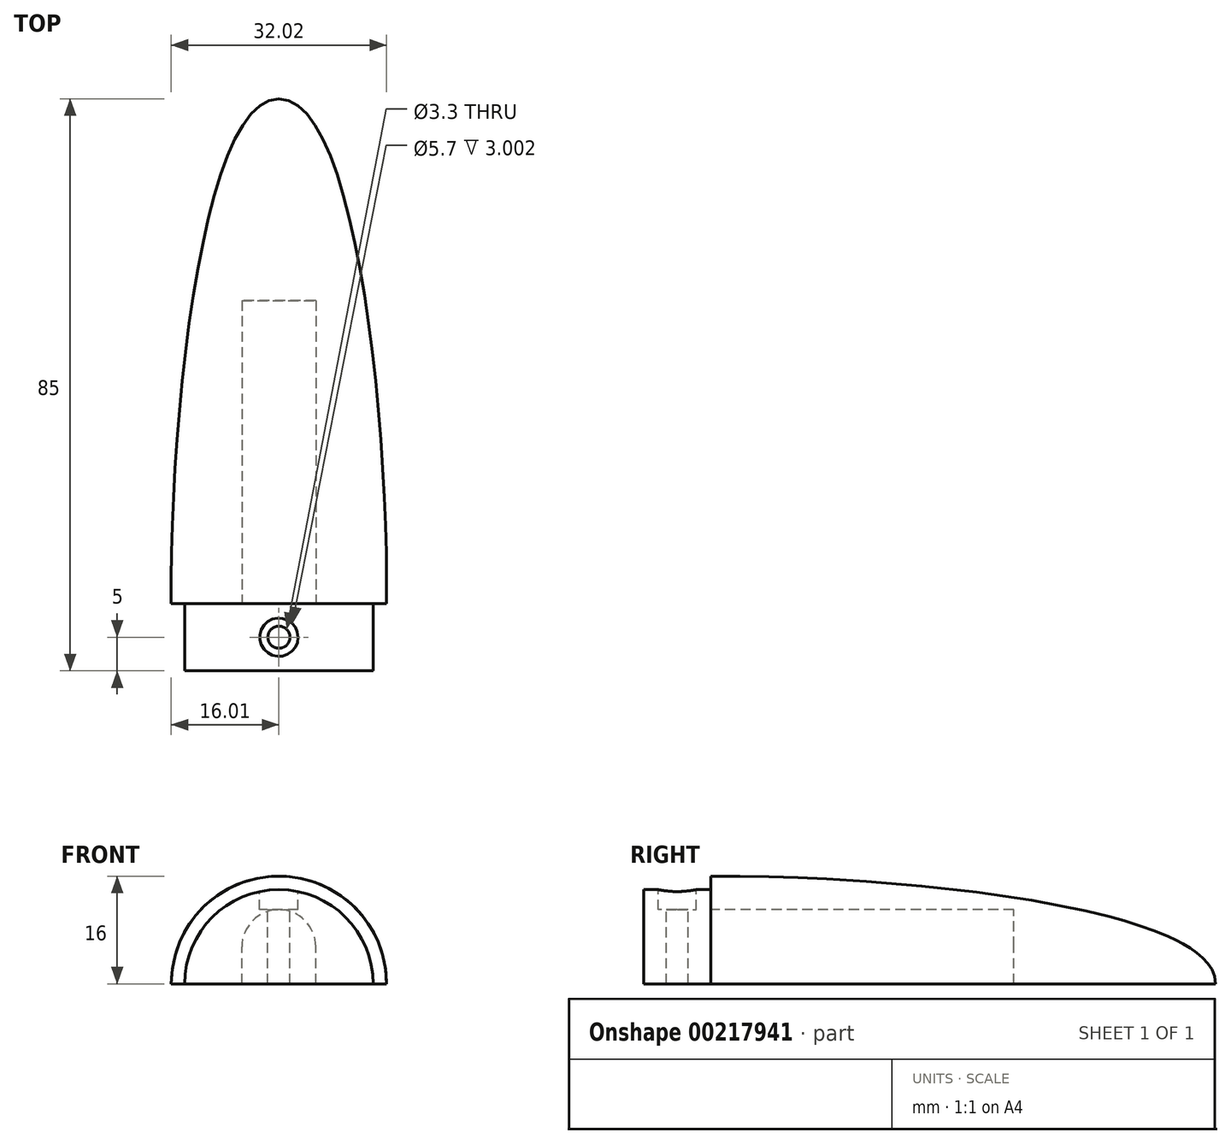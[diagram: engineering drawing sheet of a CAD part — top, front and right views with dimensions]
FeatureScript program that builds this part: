
annotation { "Feature Type Name" : "Feature", "Feature Type Description" : "" }
export const myFeature = defineFeature(function(context is Context, id is Id, definition is map)
    precondition{}
    {
        {
            var Q0;
            Q0=qCreatedBy(makeId("Top.planeOp"),FACE);
            var sketch = newSketch(context, id + "F0", { "sketchPlane" : qUnion([Q0])});
            skLineSegment(sketch, "E0.bottom", {"start": v(-5.5, 45) * mm, "end": v(5.5, 45) * mm});
            skLineSegment(sketch, "E0.top", {"start": v(-5.5, 0) * mm, "end": v(5.5, 0) * mm});
            skLineSegment(sketch, "E0.left", {"start": v(-5.5, 45) * mm, "end": v(-5.5, 0) * mm});
            skLineSegment(sketch, "E0.right", {"start": v(5.5, 45) * mm, "end": v(5.5, 0) * mm});
            skLineSegment(sketch, "E1", {"start": v(0, 0) * mm, "end": v(14, 0) * mm});
            skLineSegment(sketch, "E2", {"start": v(0, 0) * mm, "end": v(-14, 0) * mm});
            skLineSegment(sketch, "E3", {"start": v(-14, 0) * mm, "end": v(-14, 10) * mm});
            skLineSegment(sketch, "E4", {"start": v(-14, 10) * mm, "end": v(14, 10) * mm});
            skLineSegment(sketch, "E5", {"start": v(14, 10) * mm, "end": v(14, 0) * mm});
            skLineSegment(sketch, "E6", {"start": v(-5.5, 0) * mm, "end": v(-5.5, 0) * mm});
            skLineSegment(sketch, "E7", {"start": v(5.5, 0) * mm, "end": v(5.5, 0) * mm});
            skLineSegment(sketch, "E8", {"start": v(14, 10) * mm, "end": v(16, 10) * mm});
            skLineSegment(sketch, "E9", {"start": v(-14, 10) * mm, "end": v(-16, 10) * mm});
            skLineSegment(sketch, "E10", {"start": v(0, 10) * mm, "end": v(0, 85) * mm});
            skFitSpline(sketch, "E11", {"points": [v(0, 85) * mm, v(16, 10) * mm], "startDerivative": vector(34.31, 0.3) * mm, "endDerivative": vector(-0.78, -82.14) * mm});
            skFitSpline(sketch, "E12.MirrorCS", {"points": [v(0, 85) * mm, v(-16, 10) * mm], "startDerivative": vector(-34.31, 0.3) * mm, "endDerivative": vector(0.78, -82.14) * mm});
            skSolve(sketch);
        }
        {
            var Q0;
            Q0=qCreatedBy(makeId("Front.planeOp"),FACE);
            var sketch = newSketch(context, id + "F1", { "sketchPlane" : qUnion([Q0])});
            skLineSegment(sketch, "E13", {"start": v(0, 0) * mm, "end": v(0, 14.5) * mm});
            skCircle(sketch, "E14", {"center": v(0, 0) * mm, "radius": 14.5 * mm});
            skLineSegment(sketch, "E15", {"start": v(0, 0) * mm, "end": v(5.5, 0) * mm});
            skLineSegment(sketch, "E16", {"start": v(5.5, 0) * mm, "end": v(5.5, 5.5) * mm});
            skLineSegment(sketch, "E17", {"start": v(5.5, 5.5) * mm, "end": v(0, 5.5) * mm});
            skCircle(sketch, "E18", {"center": v(0, 5.5) * mm, "radius": 5.5 * mm});
            skLineSegment(sketch, "E19", {"start": v(0, 0) * mm, "end": v(-5.5, 0) * mm});
            skLineSegment(sketch, "E20", {"start": v(-5.5, 0) * mm, "end": v(-5.5, 5.5) * mm});
            skLineSegment(sketch, "E21", {"start": v(-5.5, 5.5) * mm, "end": v(0, 5.5) * mm});
            skSolve(sketch);
        }
        {
            var Q0;
            {var subQ1=sQuery(id+"F0.wireOp",EDGE,"E0.right");Q0=makeQuery(id+"F0.imprint","IMPRINT",FACE,{"disambiguationData":[TD([[makeQuery(id+"F0.imprint","IMPRINT",EDGE,{"derivedFrom":subQ1}),1.0]])]});}
            var Q1;
            {var subQ0=sQuery(id+"F0.wireOp",EDGE,"E5");Q1=makeQuery(id+"F0.imprint","IMPRINT",FACE,{"disambiguationData":[TD([[makeQuery(id+"F0.imprint","IMPRINT",EDGE,{"derivedFrom":subQ0}),-1.0]])]});}
            var Q2;
            {var subQ0=sQuery(id+"F0.wireOp",EDGE,"E8");Q2=makeQuery(id+"F0.imprint","IMPRINT",FACE,{"disambiguationData":[TD([[makeQuery(id+"F0.imprint","IMPRINT",EDGE,{"derivedFrom":subQ0}),1.0]])]});}
            var Q3;
            Q3=sQuery(id+"F0.wireOp",EDGE,"E10");
            revolve(context, id + "F2", {"entities" : qUnion([Q0, Q1, Q2]), "axis" : qUnion([Q3]), "revolveType" : RevolveType.ONE_DIRECTION, "oppositeDirection" : true, "angle" : 180 * degree});
        }
        {
            var Q0;
            {var subQ3=sQuery(id+"F1.wireOp",EDGE,"E17");Q0=makeQuery(id+"F1.imprint","IMPRINT",FACE,{"disambiguationData":[TD([[makeQuery(id+"F1.imprint","IMPRINT",EDGE,{"derivedFrom":subQ3}),1.0]])]});}
            var Q1;
            {var subQ0=sQuery(id+"F1.wireOp",EDGE,"E15");Q1=makeQuery(id+"F1.imprint","IMPRINT",FACE,{"disambiguationData":[TD([[makeQuery(id+"F1.imprint","IMPRINT",EDGE,{"derivedFrom":subQ0}),1.0]])]});}
            var Q2;
            {var subQ0=sQuery(id+"F1.wireOp",EDGE,"E19");Q2=makeQuery(id+"F1.imprint","IMPRINT",FACE,{"disambiguationData":[TD([[makeQuery(id+"F1.imprint","IMPRINT",EDGE,{"derivedFrom":subQ0}),-1.0]])]});}
            var Q3;
            {var subQ3=sQuery(id+"F1.wireOp",EDGE,"E21");Q3=makeQuery(id+"F1.imprint","IMPRINT",FACE,{"disambiguationData":[TD([[makeQuery(id+"F1.imprint","IMPRINT",EDGE,{"derivedFrom":subQ3}),-1.0]])]});}
            var Q4;
            {var subQ0=sQuery(id+"F1.wireOp",EDGE,"E21");Q4=makeQuery(id+"F1.imprint","IMPRINT",FACE,{"disambiguationData":[TD([[makeQuery(id+"F1.imprint","IMPRINT",EDGE,{"derivedFrom":subQ0}),1.0]])]});}
            var Q5;
            {var subQ0=sQuery(id+"F1.wireOp",EDGE,"E17");Q5=makeQuery(id+"F1.imprint","IMPRINT",FACE,{"disambiguationData":[TD([[makeQuery(id+"F1.imprint","IMPRINT",EDGE,{"derivedFrom":subQ0}),-1.0]])]});}
            extrude(context, id + "F3", {"entities" : qUnion([Q0, Q1, Q2, Q3, Q4, Q5]), "operationType" : NewBodyOperationType.REMOVE, "oppositeDirection" : true, "depth" : 55 * mm});
        }
        {
            var Q0;
            {var subQ0=sQuery(id+"F1.wireOp",EDGE,"E15");Q0=makeQuery(id+"F1.imprint","IMPRINT",FACE,{"disambiguationData":[TD([[makeQuery(id+"F1.imprint","IMPRINT",EDGE,{"derivedFrom":subQ0}),1.0]])]});}
            var Q1;
            {var subQ3=sQuery(id+"F1.wireOp",EDGE,"E17");Q1=makeQuery(id+"F1.imprint","IMPRINT",FACE,{"disambiguationData":[TD([[makeQuery(id+"F1.imprint","IMPRINT",EDGE,{"derivedFrom":subQ3}),1.0]])]});}
            var Q2;
            {var subQ0=sQuery(id+"F1.wireOp",EDGE,"E17");Q2=makeQuery(id+"F1.imprint","IMPRINT",FACE,{"disambiguationData":[TD([[makeQuery(id+"F1.imprint","IMPRINT",EDGE,{"derivedFrom":subQ0}),-1.0]])]});}
            var Q3;
            {var subQ0=sQuery(id+"F1.wireOp",EDGE,"E21");Q3=makeQuery(id+"F1.imprint","IMPRINT",FACE,{"disambiguationData":[TD([[makeQuery(id+"F1.imprint","IMPRINT",EDGE,{"derivedFrom":subQ0}),1.0]])]});}
            var Q4;
            {var subQ3=sQuery(id+"F1.wireOp",EDGE,"E21");Q4=makeQuery(id+"F1.imprint","IMPRINT",FACE,{"disambiguationData":[TD([[makeQuery(id+"F1.imprint","IMPRINT",EDGE,{"derivedFrom":subQ3}),-1.0]])]});}
            var Q5;
            {var subQ0=sQuery(id+"F1.wireOp",EDGE,"E19");Q5=makeQuery(id+"F1.imprint","IMPRINT",FACE,{"disambiguationData":[TD([[makeQuery(id+"F1.imprint","IMPRINT",EDGE,{"derivedFrom":subQ0}),-1.0]])]});}
            extrude(context, id + "F4", {"entities" : qUnion([Q0, Q1, Q2, Q3, Q4, Q5]), "operationType" : NewBodyOperationType.ADD, "oppositeDirection" : true, "depth" : 10 * mm});
        }
        {
            var Q0;
            Q0=makeQuery(id+"F4.boolean.opBoolean","MERGE",FACE,{"derivedFrom":[makeQuery(id+"F2.opRevolve","CAP_FACE",FACE,{"disambiguationData":[OSD([sQuery(id+"F0.wireOp",EDGE,"E0.bottom"),sQuery(id+"F0.wireOp",EDGE,"E0.right"),sQuery(id+"F0.wireOp",EDGE,"E1"),sQuery(id+"F0.wireOp",EDGE,"E5"),sQuery(id+"F0.wireOp",EDGE,"E8"),sQuery(id+"F0.wireOp",EDGE,"E10"),sQuery(id+"F0.wireOp",EDGE,"E11")])],"isStart":false}),makeQuery(id+"F4.opExtrude","SWEPT_FACE",FACE,{"disambiguationData":[OSD([sQuery(id+"F1.wireOp",EDGE,"E15"),sQuery(id+"F1.wireOp",EDGE,"E19")])]})]});
            cPlane(context, id + "F5", {"entities" : qUnion([Q0]), "cplaneType" : CPlaneType.OFFSET, "offset" : 14 * mm, "oppositeDirection" : true, "width" : 150 * mm, "height" : 150 * mm});
        }
        {
            var Q0;
            Q0=qCreatedBy(id+"F5.planeOp",FACE);
            var sketch = newSketch(context, id + "F6", { "sketchPlane" : qUnion([Q0])});
            skCircle(sketch, "E22", {"center": v(-7, -5) * mm, "radius": 1.1 * mm});
            skCircle(sketch, "E23", {"center": v(-7, -5) * mm, "radius": 2 * mm});
            skLineSegment(sketch, "E24", {"start": v(0, -7.28) * mm, "end": v(0, -2.28) * mm});
            skCircle(sketch, "E25.MirrorC", {"center": v(7, -5) * mm, "radius": 2 * mm});
            skCircle(sketch, "E26.MirrorC", {"center": v(7, -5) * mm, "radius": 1.1 * mm});
            skCircle(sketch, "E27.cCircle", {"center": v(-7, -5) * mm, "radius": 2 * mm, "construction": true});
            skLineSegment(sketch, "E27.0", {"start": v(-9, -6.15) * mm, "end": v(-9, -3.85) * mm});
            skLineSegment(sketch, "E27.1", {"start": v(-9, -3.85) * mm, "end": v(-7, -2.7) * mm});
            skLineSegment(sketch, "E27.2", {"start": v(-7, -2.7) * mm, "end": v(-5, -3.85) * mm});
            skLineSegment(sketch, "E27.3", {"start": v(-5, -3.85) * mm, "end": v(-5, -6.15) * mm});
            skLineSegment(sketch, "E27.4", {"start": v(-5, -6.15) * mm, "end": v(-7, -7.3) * mm});
            skLineSegment(sketch, "E27.5", {"start": v(-7, -7.3) * mm, "end": v(-9, -6.15) * mm});
            skPoint(sketch, "E27.0.midPoint", {"position": v(-9, -5) * mm});
            skLineSegment(sketch, "E28", {"start": v(-7, -5) * mm, "end": v(0, -5) * mm});
            skPoint(sketch, "E29.0.midPoint", {"position": v(-2.85, -5) * mm});
            skCircle(sketch, "E30", {"center": v(0, -5) * mm, "radius": 1.65 * mm});
            skCircle(sketch, "E31", {"center": v(0, -5) * mm, "radius": 2.85 * mm});
            skSolve(sketch);
        }
        {
            var Q0;
            {var subQ0=sQuery(id+"F6.wireOp",EDGE,"E24");var subQ1=makeQuery(id+"F6.imprint","INTERSECT",VERTEX,{"derivedFrom":[subQ0,sQuery(id+"F6.wireOp",EDGE,"E28")]});Q0=makeQuery(id+"F6.imprint","IMPRINT",FACE,{"disambiguationData":[TD([[makeQuery(id+"F6.imprint","IMPRINT",EDGE,{"disambiguationData":[TD([[subQ1,1.0]])],"derivedFrom":subQ0}),-1.0]])]});}
            var Q1;
            {var subQ0=sQuery(id+"F6.wireOp",EDGE,"E28");var subQ1=sQuery(id+"F6.wireOp",EDGE,"E24");var subQ2=makeQuery(id+"F6.imprint","INTERSECT",VERTEX,{"derivedFrom":[subQ1,subQ0]});Q1=makeQuery(id+"F6.imprint","IMPRINT",FACE,{"disambiguationData":[TD([[makeQuery(id+"F6.imprint","IMPRINT",EDGE,{"disambiguationData":[TD([[subQ2,-1.0]])],"derivedFrom":subQ1}),1.0]])]});}
            var Q2;
            {var subQ0=sQuery(id+"F6.wireOp",EDGE,"E28");var subQ1=sQuery(id+"F6.wireOp",EDGE,"E24");var subQ2=makeQuery(id+"F6.imprint","INTERSECT",VERTEX,{"derivedFrom":[subQ1,subQ0]});Q2=makeQuery(id+"F6.imprint","IMPRINT",FACE,{"disambiguationData":[TD([[makeQuery(id+"F6.imprint","IMPRINT",EDGE,{"disambiguationData":[TD([[subQ2,1.0]])],"derivedFrom":subQ1}),1.0]])]});}
            extrude(context, id + "F7", {"entities" : qUnion([Q0, Q1, Q2]), "operationType" : NewBodyOperationType.REMOVE, "depth" : 25 * mm});
        }
        {
            var Q0;
            Q0=makeQuery(id+"F6.imprint","IMPRINT",FACE,{"disambiguationData":[TD([[makeQuery(id+"F6.imprint","IMPRINT",EDGE,{"derivedFrom":sQuery(id+"F6.wireOp",EDGE,"E31")}),1.0]])]});
            extrude(context, id + "F8", {"entities" : qUnion([Q0]), "operationType" : NewBodyOperationType.REMOVE, "depth" : 3 * mm});
        }
    });
